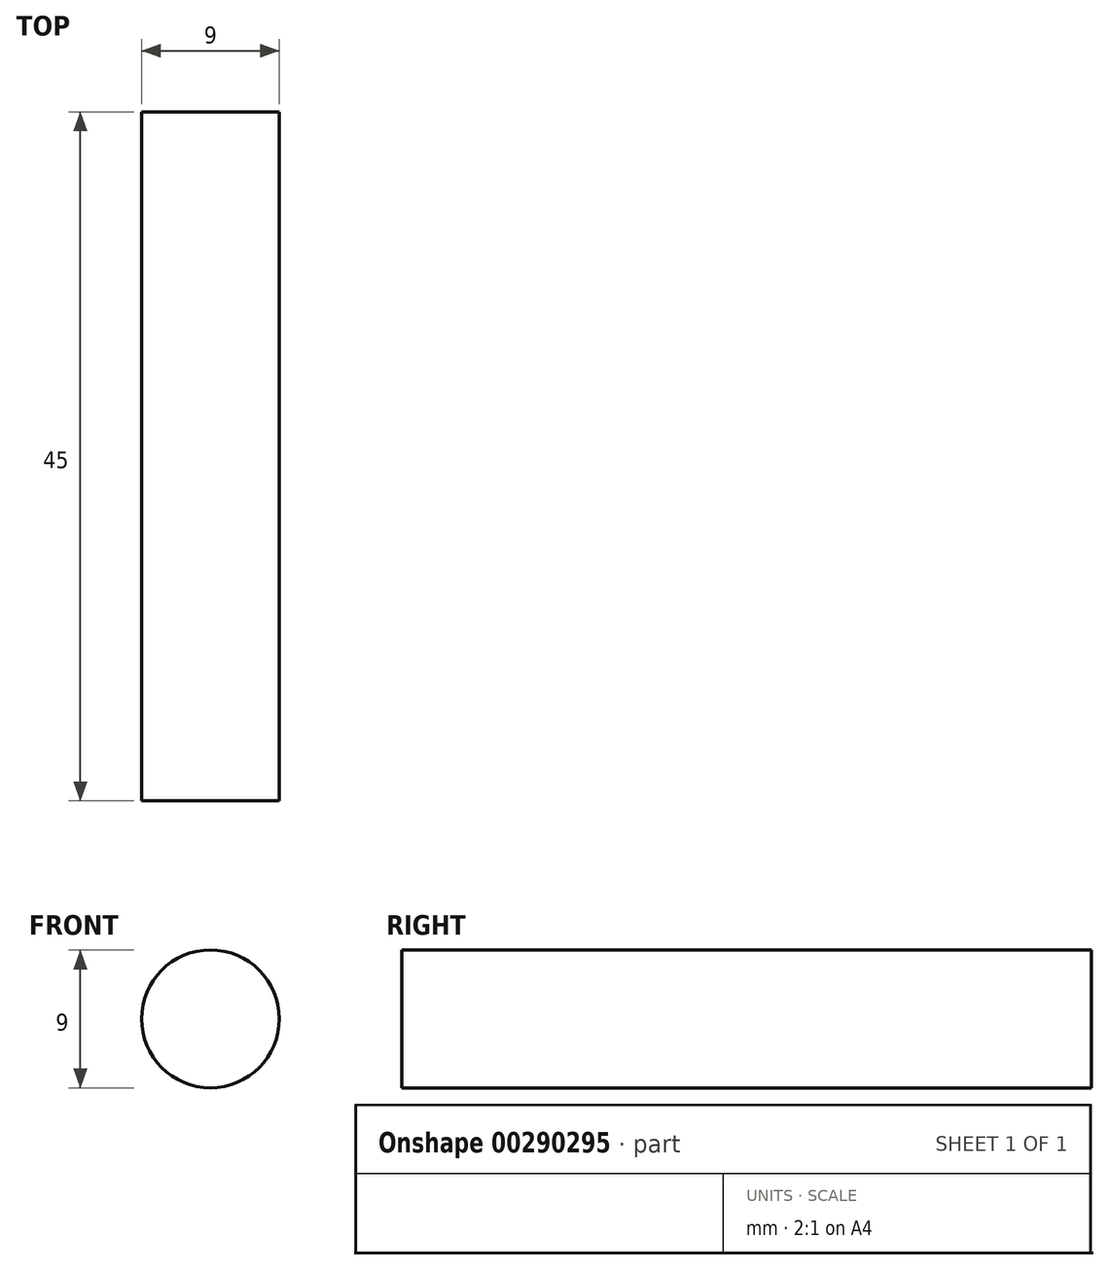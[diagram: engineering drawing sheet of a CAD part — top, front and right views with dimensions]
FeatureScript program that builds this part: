
annotation { "Feature Type Name" : "Feature", "Feature Type Description" : "" }
export const myFeature = defineFeature(function(context is Context, id is Id, definition is map)
    precondition{}
    {
        {
            var Q0;
            Q0=qCreatedBy(makeId("Front.planeOp"),FACE);
            var sketch = newSketch(context, id + "F0", { "sketchPlane" : qUnion([Q0])});
            skCircle(sketch, "E0", {"center": v(0, 0) * mm, "radius": 4.5 * mm});
            skSolve(sketch);
        }
        {
            var Q0;
            Q0 = qSketchRegion(id + "F0", true);
            extrude(context, id + "F1", {"entities" : qUnion([Q0]), "depth" : 45 * mm});
        }
    });
